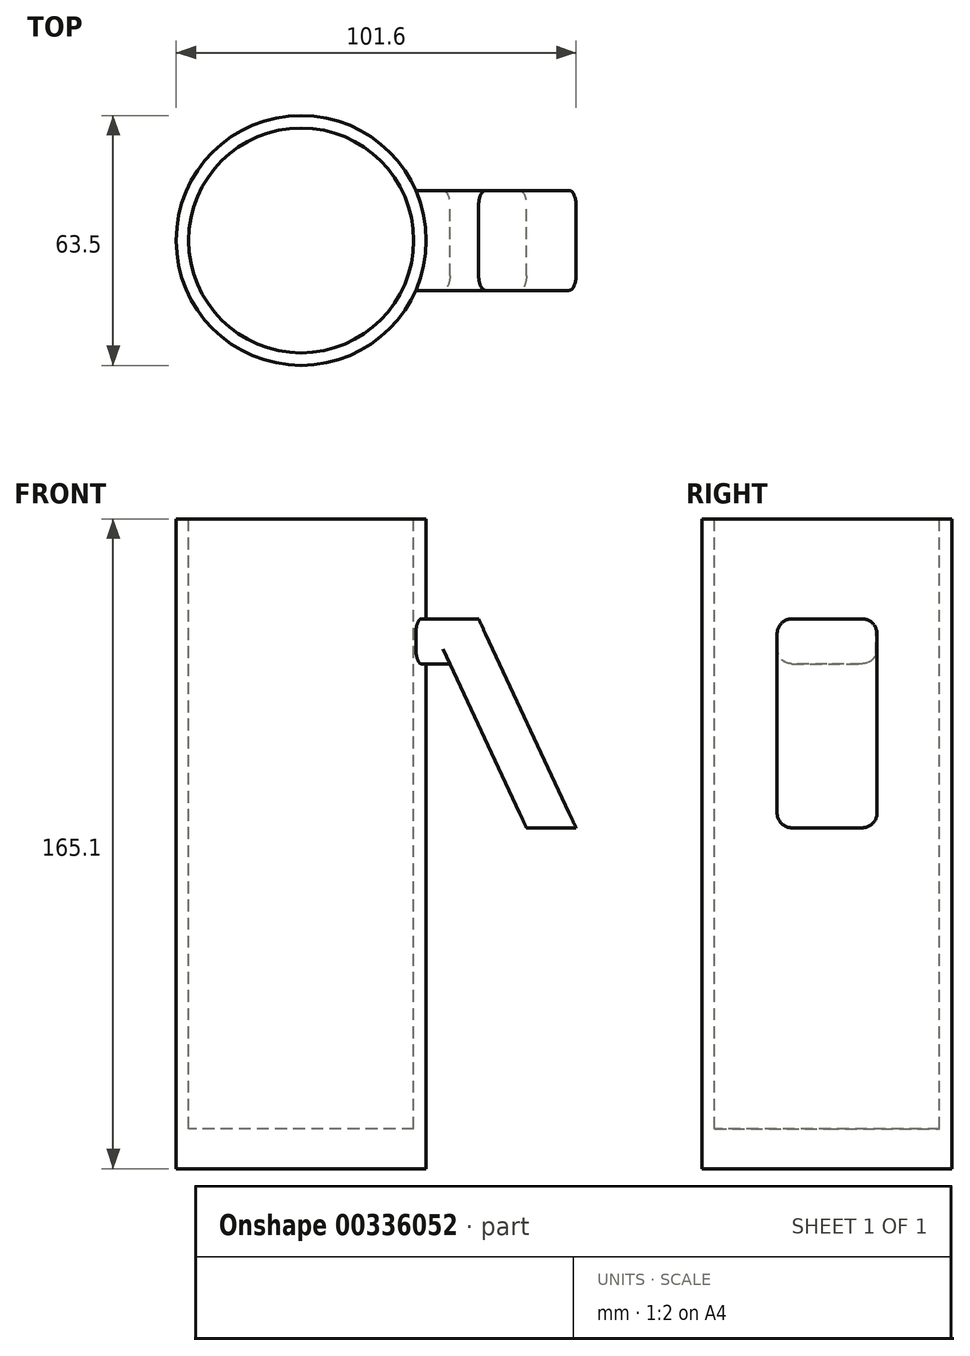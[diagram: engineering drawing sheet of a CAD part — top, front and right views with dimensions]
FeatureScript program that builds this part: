
annotation { "Feature Type Name" : "Feature", "Feature Type Description" : "" }
export const myFeature = defineFeature(function(context is Context, id is Id, definition is map)
    precondition{}
    {
        {
            var Q0;
            Q0=qCreatedBy(makeId("Front.planeOp"),FACE);
            var sketch = newSketch(context, id + "F0", { "sketchPlane" : qUnion([Q0])});
            skLineSegment(sketch, "E0.bottom", {"start": v(0, 0) * mm, "end": v(31.75, 0) * mm});
            skLineSegment(sketch, "E0.top", {"start": v(0, -165.1) * mm, "end": v(31.75, -165.1) * mm});
            skLineSegment(sketch, "E0.left", {"start": v(0, 0) * mm, "end": v(0, -165.1) * mm});
            skLineSegment(sketch, "E0.right", {"start": v(31.75, 0) * mm, "end": v(31.75, -165.1) * mm});
            skLineSegment(sketch, "E1", {"start": v(29.21, -25.4) * mm, "end": v(45.09, -25.4) * mm});
            skLineSegment(sketch, "E2", {"start": v(45.08, -25.4) * mm, "end": v(69.85, -78.5) * mm});
            skLineSegment(sketch, "E3", {"start": v(69.85, -78.5) * mm, "end": v(57.24, -78.5) * mm});
            skLineSegment(sketch, "E4", {"start": v(57.24, -78.5) * mm, "end": v(37.8, -36.83) * mm});
            skLineSegment(sketch, "E5", {"start": v(37.8, -36.83) * mm, "end": v(29.21, -36.83) * mm});
            skLineSegment(sketch, "E6", {"start": v(29.21, -25.4) * mm, "end": v(29.21, -36.83) * mm});
            skSolve(sketch);
        }
        {
            var Q0;
            {var subQ1=sQuery(id+"F0.wireOp",EDGE,"E0.bottom");Q0=makeQuery(id+"F0.imprint","IMPRINT",FACE,{"disambiguationData":[TD([[makeQuery(id+"F0.imprint","IMPRINT",EDGE,{"derivedFrom":subQ1}),-1.0]])]});}
            var Q1;
            {var subQ5=sQuery(id+"F0.wireOp",EDGE,"E6");Q1=makeQuery(id+"F0.imprint","IMPRINT",FACE,{"disambiguationData":[TD([[makeQuery(id+"F0.imprint","IMPRINT",EDGE,{"derivedFrom":subQ5}),1.0]])]});}
            var Q2;
            Q2=sQuery(id+"F0.wireOp",EDGE,"E0.left");
            revolve(context, id + "F1", {"entities" : qUnion([Q0, Q1]), "axis" : qUnion([Q2]), "revolveType" : RevolveType.FULL});
        }
        {
            var Q0;
            {var subQ0=sQuery(id+"F0.wireOp",EDGE,"E2");Q0=makeQuery(id+"F0.imprint","IMPRINT",FACE,{"disambiguationData":[TD([[makeQuery(id+"F0.imprint","IMPRINT",EDGE,{"derivedFrom":subQ0}),-1.0]])]});}
            var Q1;
            {var subQ5=sQuery(id+"F0.wireOp",EDGE,"E6");Q1=makeQuery(id+"F0.imprint","IMPRINT",FACE,{"disambiguationData":[TD([[makeQuery(id+"F0.imprint","IMPRINT",EDGE,{"derivedFrom":subQ5}),1.0]])]});}
            extrude(context, id + "F2", {"entities" : qUnion([Q0, Q1]), "operationType" : NewBodyOperationType.ADD, "endBound" : BoundingType.SYMMETRIC, "depth" : 25.4 * mm});
        }
        {
            var Q0;
            Q0=makeQuery(id+"F2.opExtrude","CAP_EDGE",EDGE,{"disambiguationData":[OSD([sQuery(id+"F0.wireOp",EDGE,"E1")])],"isStart":false});
            var Q1;
            Q1=makeQuery(id+"F2.opExtrude","CAP_EDGE",EDGE,{"disambiguationData":[OSD([sQuery(id+"F0.wireOp",EDGE,"E1")])],"isStart":true});
            var Q2;
            Q2=makeQuery(id+"F2.opExtrude","CAP_EDGE",EDGE,{"disambiguationData":[OSD([sQuery(id+"F0.wireOp",EDGE,"E5")])],"isStart":true});
            var Q3;
            Q3=makeQuery(id+"F2.opExtrude","CAP_EDGE",EDGE,{"disambiguationData":[OSD([sQuery(id+"F0.wireOp",EDGE,"E5")])],"isStart":false});
            var Q4;
            Q4=makeQuery(id+"F2.opExtrude","CAP_EDGE",EDGE,{"disambiguationData":[OSD([sQuery(id+"F0.wireOp",EDGE,"E3")])],"isStart":false});
            var Q5;
            Q5=makeQuery(id+"F2.opExtrude","CAP_EDGE",EDGE,{"disambiguationData":[OSD([sQuery(id+"F0.wireOp",EDGE,"E3")])],"isStart":true});
            fillet(context, id + "F3", {"entities" : qUnion([Q0, Q1, Q2, Q3, Q4, Q5]), "radius" : 3.8 * mm, "tangentPropagation" : true, "allowEdgeOverflow" : false});
        }
        {
            var Q0;
            Q0=makeQuery(id+"F1.opRevolve","SWEPT_FACE",FACE,{"disambiguationData":[OSD([sQuery(id+"F0.wireOp",EDGE,"E0.bottom")])]});
            var sketch = newSketch(context, id + "F4", { "sketchPlane" : qUnion([Q0])});
            skCircle(sketch, "E7", {"center": v(0, 0) * mm, "radius": 28.58 * mm});
            skSolve(sketch);
        }
        {
            var Q0;
            Q0=makeQuery(id+"F4.imprint","IMPRINT",FACE,{"disambiguationData":[TD([[makeQuery(id+"F4.imprint","IMPRINT",EDGE,{"derivedFrom":sQuery(id+"F4.wireOp",EDGE,"E7")}),1.0]])]});
            extrude(context, id + "F5", {"entities" : qUnion([Q0]), "operationType" : NewBodyOperationType.REMOVE, "oppositeDirection" : true, "depth" : 76.2 * mm});
        }
        {
            var Q0;
            Q0=makeQuery(id+"F5.boolean.opBoolean","COPY",FACE,{"derivedFrom":makeQuery(id+"F5.opExtrude","CAP_FACE",FACE,{"disambiguationData":[OSD([sQuery(id+"F4.wireOp",EDGE,"E7")])],"isStart":false})});
            extrude(context, id + "F6", {"entities" : qUnion([Q0]), "operationType" : NewBodyOperationType.REMOVE, "oppositeDirection" : true, "depth" : 78.74 * mm});
        }
    });
